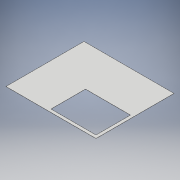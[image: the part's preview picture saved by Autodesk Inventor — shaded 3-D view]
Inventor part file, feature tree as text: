
AUTODESK INVENTOR PART (.ipt)
format: ipt  version: 2017 (Build 210142000, 142)  size: 107,520 bytes
history: native  units: mm
features: sketch x2, other x2, sheet_metal_op x1
ambient origin geometry x8: Origin, YZ Plane, XZ Plane, XY Plane, X Axis, Y Axis, Z Axis, Center Point
bodies: Solid1 (feature_tree)
feature tree (5):
  sheet_metal_op  "Face1"
  sketch  "Sketch1"  dims[d0=300.0mm]
  other  "Plate1"
  sketch  "Sketch3"  dims[d1=260.0mm d2=0.5mm d3=280.0mm d4=240.0mm d5=150.0mm d6=115.0mm d7=0.5mm d8=0.0mm]
  other  "Cut1"
